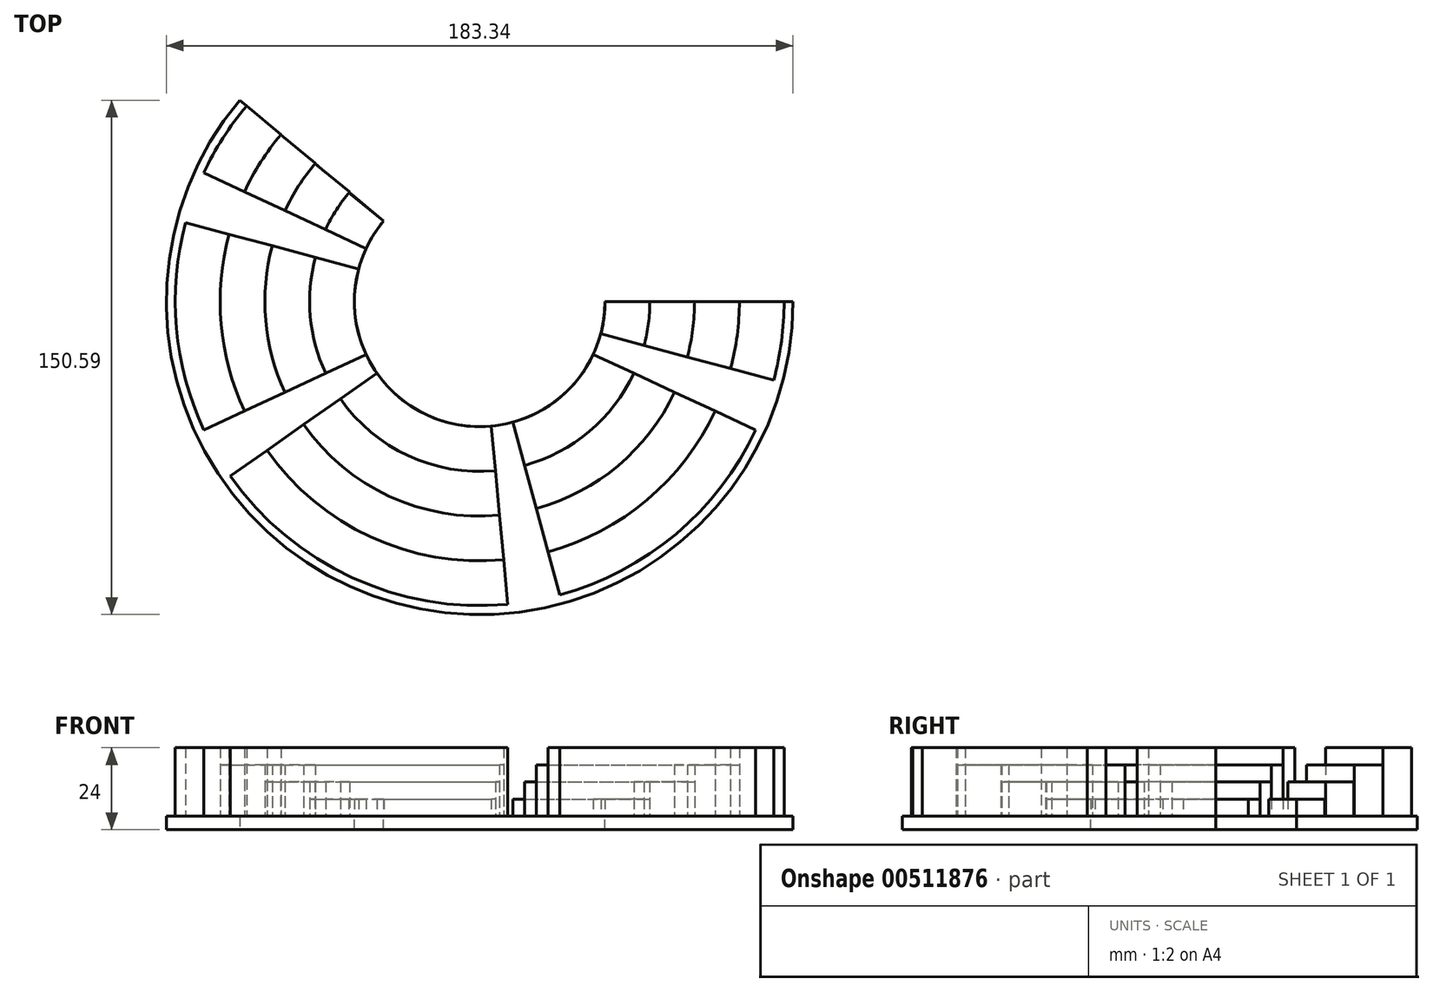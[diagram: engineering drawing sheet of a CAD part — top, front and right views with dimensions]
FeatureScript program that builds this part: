
annotation { "Feature Type Name" : "Feature", "Feature Type Description" : "" }
export const myFeature = defineFeature(function(context is Context, id is Id, definition is map)
    precondition{}
    {
        {
            var Q0;
            Q0=qCreatedBy(makeId("Front.planeOp"),FACE);
            var sketch = newSketch(context, id + "F0", { "sketchPlane" : qUnion([Q0])});
            skLineSegment(sketch, "E0.bottom", {"start": v(0, 0) * mm, "end": v(91.67, 0) * mm});
            skLineSegment(sketch, "E0.top", {"start": v(0, -4) * mm, "end": v(91.67, -4) * mm});
            skLineSegment(sketch, "E0.left", {"start": v(0, 0) * mm, "end": v(0, -4) * mm});
            skLineSegment(sketch, "E0.right", {"start": v(91.67, 0) * mm, "end": v(91.67, -4) * mm});
            skSolve(sketch);
        }
        {
            var Q0;
            Q0 = qSketchRegion(id + "F0", true);
            var Q1;
            Q1=sQuery(id+"F0.wireOp",EDGE,"E0.left");
            revolve(context, id + "F1", {"entities" : qUnion([Q0]), "axis" : qUnion([Q1]), "revolveType" : RevolveType.ONE_DIRECTION, "angle" : 220 * degree});
        }
        {
            var Q0;
            Q0=qCreatedBy(makeId("Top.planeOp"),FACE);
            var sketch = newSketch(context, id + "F2", { "sketchPlane" : qUnion([Q0])});
            skCircle(sketch, "E1", {"center": v(0, 0) * mm, "radius": 36.67 * mm});
            skSolve(sketch);
        }
        {
            var Q0;
            Q0 = qSketchRegion(id + "F2", true);
            extrude(context, id + "F3", {"entities" : qUnion([Q0]), "operationType" : NewBodyOperationType.REMOVE, "endBound" : BoundingType.SYMMETRIC, "oppositeDirection" : true, "depth" : 25 * mm});
        }
        {
            var Q0;
            Q0=qCreatedBy(makeId("Top.planeOp"),FACE);
            var sketch = newSketch(context, id + "F4", { "sketchPlane" : qUnion([Q0])});
            skLineSegment(sketch, "E2", {"start": v(-28.08, 23.56) * mm, "end": v(-28.09, 23.57) * mm, "construction": true});
            skLineSegment(sketch, "E3", {"start": v(-28.08, 23.56) * mm, "end": v(-28.09, 23.57) * mm});
            skArc(sketch, "E4", {"start": v(-28.09, 23.57) * mm, "mid": v(-12.54, -34.46) * mm, "end": v(36.67, 0) * mm});
            skArc(sketch, "E5", {"start": v(-38.25, 31.83) * mm, "mid": v(-16.92, -46.8) * mm, "end": v(49.76, 0) * mm});
            skLineSegment(sketch, "E6", {"start": v(-28.08, 23.56) * mm, "end": v(-38.25, 31.83) * mm});
            skLineSegment(sketch, "E7", {"start": v(36.67, 0) * mm, "end": v(49.76, 0) * mm});
            skSolve(sketch);
        }
        {
            var Q0;
            Q0 = qSketchRegion(id + "F4", true);
            extrude(context, id + "F5", {"entities" : qUnion([Q0]), "depth" : 5 * mm});
        }
        {
            var Q0;
            Q0=qCreatedBy(makeId("Top.planeOp"),FACE);
            var sketch = newSketch(context, id + "F6", { "sketchPlane" : qUnion([Q0])});
            skArc(sketch, "E8", {"start": v(-38, 32.13) * mm, "mid": v(-17.1, -46.73) * mm, "end": v(49.76, 0) * mm});
            skArc(sketch, "E9", {"start": v(-48.2, 40.34) * mm, "mid": v(-21.46, -59.08) * mm, "end": v(62.86, 0) * mm});
            skLineSegment(sketch, "E10", {"start": v(-38, 32.13) * mm, "end": v(-48.2, 40.34) * mm});
            skLineSegment(sketch, "E11", {"start": v(49.76, 0) * mm, "end": v(62.86, 0) * mm});
            skSolve(sketch);
        }
        {
            var Q0;
            Q0 = qSketchRegion(id + "F6", true);
            extrude(context, id + "F7", {"entities" : qUnion([Q0]), "depth" : 10 * mm});
        }
        {
            var Q0;
            Q0=qCreatedBy(makeId("Top.planeOp"),FACE);
            var sketch = newSketch(context, id + "F8", { "sketchPlane" : qUnion([Q0])});
            skArc(sketch, "E12", {"start": v(-58.2, 48.81) * mm, "mid": v(-25.97, -71.37) * mm, "end": v(75.95, 0) * mm});
            skArc(sketch, "E13", {"start": v(-48.11, 40.45) * mm, "mid": v(-21.53, -59.06) * mm, "end": v(62.86, 0) * mm});
            skLineSegment(sketch, "E14", {"start": v(62.86, 0) * mm, "end": v(75.95, 0) * mm});
            skLineSegment(sketch, "E15", {"start": v(-48.11, 40.45) * mm, "end": v(-58.2, 48.81) * mm});
            skSolve(sketch);
        }
        {
            var Q0;
            Q0 = qSketchRegion(id + "F8", true);
            extrude(context, id + "F9", {"entities" : qUnion([Q0]), "depth" : 15 * mm});
        }
        {
            var Q0;
            Q0=qCreatedBy(makeId("Top.planeOp"),FACE);
            var sketch = newSketch(context, id + "F10", { "sketchPlane" : qUnion([Q0])});
            skArc(sketch, "E16", {"start": v(-58.18, 48.82) * mm, "mid": v(-25.98, -71.37) * mm, "end": v(75.95, 0) * mm});
            skArc(sketch, "E17", {"start": v(-68.21, 57.24) * mm, "mid": v(-30.46, -83.68) * mm, "end": v(89.05, 0) * mm});
            skLineSegment(sketch, "E18", {"start": v(75.95, 0) * mm, "end": v(89.05, 0) * mm});
            skLineSegment(sketch, "E19", {"start": v(-58.18, 48.82) * mm, "end": v(-68.21, 57.24) * mm});
            skSolve(sketch);
        }
        {
            var Q0;
            Q0 = qSketchRegion(id + "F10", true);
            extrude(context, id + "F11", {"entities" : qUnion([Q0]), "depth" : 20 * mm});
        }
        {
            var Q0;
            Q0=qCreatedBy(makeId("Top.planeOp"),FACE);
            var sketch = newSketch(context, id + "F12", { "sketchPlane" : qUnion([Q0])});
            skLineSegment(sketch, "E20", {"start": v(0, 0) * mm, "end": v(-88.8, 41.41) * mm});
            skLineSegment(sketch, "E21", {"start": v(0, 0) * mm, "end": v(-94.33, 25.28) * mm});
            skLineSegment(sketch, "E22", {"start": v(-94.33, 25.28) * mm, "end": v(-88.8, 41.41) * mm});
            skLineSegment(sketch, "E23.MirrorCS", {"start": v(0, 0) * mm, "end": v(88.5, -41.27) * mm});
            skLineSegment(sketch, "E24", {"start": v(0, 0) * mm, "end": v(8.25, 17.7) * mm, "construction": true});
            skPoint(sketch, "E25.orphan", {"position": v(88.8, -41.41) * mm});
            skPoint(sketch, "E26.MirrorCS.start.orphan", {"position": v(0, 0) * mm});
            skLineSegment(sketch, "E27.MirrorCS", {"start": v(0, 0) * mm, "end": v(88.8, -41.41) * mm});
            skPoint(sketch, "E28.MirrorCS.end.orphan", {"position": v(80, -56.01) * mm});
            skLineSegment(sketch, "E29", {"start": v(0, 0) * mm, "end": v(94.65, -25.36) * mm});
            skLineSegment(sketch, "E30", {"start": v(88.5, -41.27) * mm, "end": v(94.65, -25.36) * mm});
            skSolve(sketch);
        }
        {
            var Q0;
            {var subQ0=sQuery(id+"F12.wireOp",EDGE,"E29");Q0=makeQuery(id+"F12.imprint","IMPRINT",FACE,{"disambiguationData":[TD([[makeQuery(id+"F12.imprint","IMPRINT",EDGE,{"derivedFrom":subQ0}),-1.0]])]});}
            var Q1;
            Q1=makeQuery(id+"F12.imprint","IMPRINT",FACE,{"disambiguationData":[TD([[makeQuery(id+"F12.imprint","IMPRINT",EDGE,{"derivedFrom":sQuery(id+"F12.wireOp",EDGE,"E20")}),1.0]])]});
            extrude(context, id + "F13", {"entities" : qUnion([Q0, Q1]), "operationType" : NewBodyOperationType.REMOVE, "depth" : 29 * mm});
        }
        {
            var Q0;
            Q0=qCreatedBy(makeId("Top.planeOp"),FACE);
            var sketch = newSketch(context, id + "F14", { "sketchPlane" : qUnion([Q0])});
            skLineSegment(sketch, "E31", {"start": v(0, 0) * mm, "end": v(-88.82, -41.42) * mm});
            skLineSegment(sketch, "E32", {"start": v(0, 0) * mm, "end": v(-80.28, -56.21) * mm});
            skLineSegment(sketch, "E33", {"start": v(-88.82, -41.42) * mm, "end": v(-80.28, -56.21) * mm});
            skPoint(sketch, "E34.MirrorCS.end.orphan", {"position": v(80.28, -56.21) * mm});
            skPoint(sketch, "E35.MirrorCS.end.orphan", {"position": v(88.82, -41.42) * mm});
            skPoint(sketch, "E35.MirrorCS.start.orphan", {"position": v(0, 0) * mm});
            skPoint(sketch, "E36.start.orphan", {"position": v(0, -1.97) * mm});
            skLineSegment(sketch, "E37", {"start": v(0, 0) * mm, "end": v(8.82, -95.69) * mm});
            skLineSegment(sketch, "E38", {"start": v(8.82, -95.69) * mm, "end": v(25.05, -91.8) * mm});
            skLineSegment(sketch, "E39", {"start": v(25.05, -91.8) * mm, "end": v(0, 0) * mm});
            skSolve(sketch);
        }
        {
            var Q0;
            Q0 = qSketchRegion(id + "F14", true);
            extrude(context, id + "F15", {"entities" : qUnion([Q0]), "operationType" : NewBodyOperationType.REMOVE, "depth" : 25 * mm});
        }
    });
